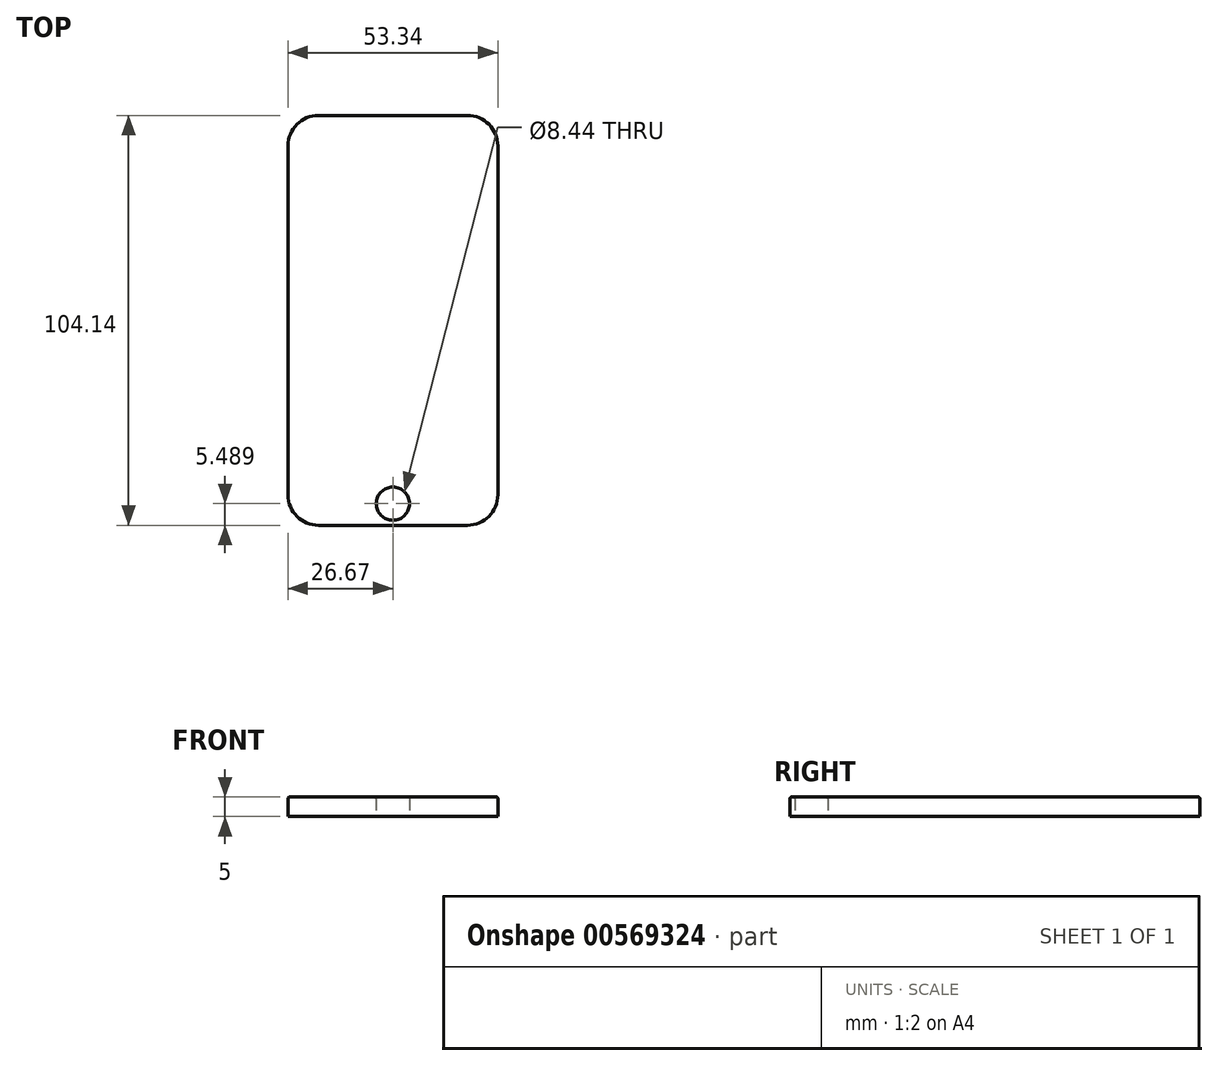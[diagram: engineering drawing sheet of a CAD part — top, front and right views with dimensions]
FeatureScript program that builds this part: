
annotation { "Feature Type Name" : "Feature", "Feature Type Description" : "" }
export const myFeature = defineFeature(function(context is Context, id is Id, definition is map)
    precondition{}
    {
        {
            var Q0;
            Q0=qCreatedBy(makeId("Top.planeOp"),FACE);
            var sketch = newSketch(context, id + "F0", { "sketchPlane" : qUnion([Q0])});
            skLineSegment(sketch, "E0.bottom", {"start": v(18.9, 52.07) * mm, "end": v(-18.9, 52.07) * mm});
            skLineSegment(sketch, "E0.top", {"start": v(18.9, -52.07) * mm, "end": v(-18.9, -52.07) * mm});
            skLineSegment(sketch, "E0.left", {"start": v(26.67, 44.3) * mm, "end": v(26.67, -44.3) * mm});
            skLineSegment(sketch, "E0.right", {"start": v(-26.67, 44.3) * mm, "end": v(-26.67, -44.3) * mm});
            skPoint(sketch, "E0.middle", {"position": v(0, 0) * mm});
            skPoint(sketch, "E1.visualSharp", {"position": v(-26.67, 52.07) * mm});
            skArc(sketch, "E1.filletArc", {"start": v(-18.9, 52.07) * mm, "mid": v(-24.4, 49.8) * mm, "end": v(-26.67, 44.3) * mm});
            skPoint(sketch, "E2.visualSharp", {"position": v(26.67, 52.07) * mm});
            skArc(sketch, "E2.filletArc", {"start": v(26.67, 44.3) * mm, "mid": v(24.4, 49.8) * mm, "end": v(18.9, 52.07) * mm});
            skPoint(sketch, "E3.visualSharp", {"position": v(26.67, -52.07) * mm});
            skArc(sketch, "E3.filletArc", {"start": v(18.9, -52.07) * mm, "mid": v(24.4, -49.8) * mm, "end": v(26.67, -44.3) * mm});
            skPoint(sketch, "E4.visualSharp", {"position": v(-26.67, -52.07) * mm});
            skArc(sketch, "E4.filletArc", {"start": v(-26.67, -44.3) * mm, "mid": v(-24.4, -49.8) * mm, "end": v(-18.9, -52.07) * mm});
            skCircle(sketch, "E5", {"center": v(0, -46.58) * mm, "radius": 4.22 * mm});
            skSolve(sketch);
        }
        {
            var Q0;
            Q0=makeQuery(id+"F0.imprint","IMPRINT",FACE,{"disambiguationData":[TD([[makeQuery(id+"F0.imprint","IMPRINT",EDGE,{"derivedFrom":sQuery(id+"F0.wireOp",EDGE,"E0.bottom")}),1.0]])]});
            extrude(context, id + "F1", {"entities" : qUnion([Q0]), "depth" : 5 * mm, "offsetDistance" : 25 * mm});
        }
        {
            var Q0;
            Q0=makeQuery(id+"F1.opExtrude","CAP_FACE",FACE,{"disambiguationData":[OSD([sQuery(id+"F0.wireOp",EDGE,"E0.bottom"),sQuery(id+"F0.wireOp",EDGE,"E0.top"),sQuery(id+"F0.wireOp",EDGE,"E0.left"),sQuery(id+"F0.wireOp",EDGE,"E0.right"),sQuery(id+"F0.wireOp",EDGE,"E1.filletArc"),sQuery(id+"F0.wireOp",EDGE,"E2.filletArc"),sQuery(id+"F0.wireOp",EDGE,"E3.filletArc"),sQuery(id+"F0.wireOp",EDGE,"E4.filletArc")])],"isStart":false});
            fillet(context, id + "F2", {"entities" : qUnion([Q0]), "radius" : 0.5 * mm, "tangentPropagation" : true, "allowEdgeOverflow" : false});
        }
    });
